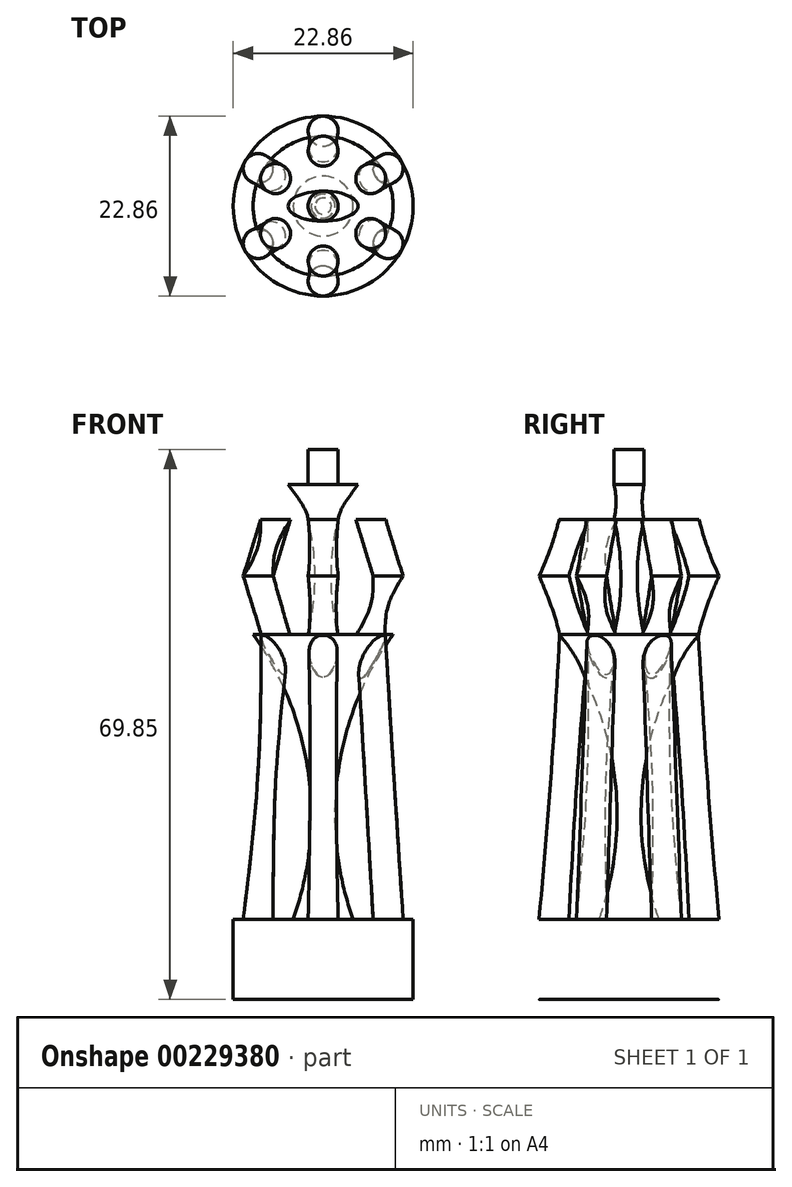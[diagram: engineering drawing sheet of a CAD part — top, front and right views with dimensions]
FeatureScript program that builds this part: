
annotation { "Feature Type Name" : "Feature", "Feature Type Description" : "" }
export const myFeature = defineFeature(function(context is Context, id is Id, definition is map)
    precondition{}
    {
        {
            var Q0;
            Q0=qCreatedBy(makeId("Top.planeOp"),FACE);
            var sketch = newSketch(context, id + "F0", { "sketchPlane" : qUnion([Q0])});
            skCircle(sketch, "E0", {"center": v(0, 0) * mm, "radius": 11.43 * mm});
            skSolve(sketch);
        }
        {
            var Q0;
            Q0=qSketchRegion(id+"F0",true);
            extrude(context, id + "F1", {"entities" : qUnion([Q0]), "depth" : 10.16 * mm});
        }
        {
            var Q0;
            Q0=makeQuery(id+"F1.opExtrude","CAP_FACE",FACE,{"disambiguationData":[OSD([sQuery(id+"F0.wireOp",EDGE,"E0")])],"isStart":false});
            var sketch = newSketch(context, id + "F2", { "sketchPlane" : qUnion([Q0])});
            skCircle(sketch, "E1", {"center": v(0, -9.53) * mm, "radius": 1.9 * mm});
            skCircle(sketch, "E2.1.0", {"center": v(8.25, -4.76) * mm, "radius": 1.9 * mm});
            skCircle(sketch, "E2.2.0", {"center": v(8.25, 4.76) * mm, "radius": 1.9 * mm});
            skCircle(sketch, "E2.3.0", {"center": v(0, 9.53) * mm, "radius": 1.9 * mm});
            skCircle(sketch, "E2.4.0", {"center": v(-8.25, 4.76) * mm, "radius": 1.9 * mm});
            skCircle(sketch, "E2.5.0", {"center": v(-8.25, -4.76) * mm, "radius": 1.9 * mm});
            skPoint(sketch, "E2.center", {"position": v(0, 0) * mm});
            skSolve(sketch);
        }
        {
            var Q0;
            Q0=qCreatedBy(makeId("Top.planeOp"),FACE);
            cPlane(context, id + "F3", {"entities" : qUnion([Q0]), "cplaneType" : CPlaneType.OFFSET, "offset" : 60.96 * mm, "width" : 152.4 * mm, "height" : 152.4 * mm});
        }
        {
            var Q0;
            Q0=qCreatedBy(makeId("Right.planeOp"),FACE);
            var sketch = newSketch(context, id + "F4", { "sketchPlane" : qUnion([Q0])});
            skLineSegment(sketch, "E3", {"start": v(0, 0) * mm, "end": v(0, 10.16) * mm});
            skLineSegment(sketch, "E4", {"start": v(0, 10.16) * mm, "end": v(0, 46.36) * mm});
            skLineSegment(sketch, "E5", {"start": v(0, 46.36) * mm, "end": v(8.9, 46.36) * mm});
            skLineSegment(sketch, "E6", {"start": v(0, 10.16) * mm, "end": v(3.81, 10.16) * mm});
            skArc(sketch, "E7", {"start": v(8.89, 46.36) * mm, "mid": v(1.9, 28.88) * mm, "end": v(3.81, 10.16) * mm});
            skSolve(sketch);
        }
        {
            var Q0;
            Q0=makeQuery(id+"F4.imprint","IMPRINT",FACE,{"disambiguationData":[TD([[makeQuery(id+"F4.imprint","IMPRINT",EDGE,{"derivedFrom":sQuery(id+"F4.wireOp",EDGE,"E4")}),-1.0]])]});
            var Q1;
            Q1=sQuery(id+"F4.wireOp",EDGE,"E4");
            revolve(context, id + "F5", {"operationType" : NewBodyOperationType.ADD, "entities" : qUnion([Q0]), "axis" : qUnion([Q1]), "revolveType" : RevolveType.FULL});
        }
        {
            var Q0;
            Q0=makeQuery(id+"F5.opRevolve","SWEPT_FACE",FACE,{"disambiguationData":[OSD([sQuery(id+"F4.wireOp",EDGE,"E5")])]});
            var sketch = newSketch(context, id + "F6", { "sketchPlane" : qUnion([Q0])});
            skCircle(sketch, "E8", {"center": v(0, -6.99) * mm, "radius": 1.83 * mm});
            skCircle(sketch, "E9.1.0", {"center": v(6.05, -3.5) * mm, "radius": 1.83 * mm});
            skCircle(sketch, "E9.2.0", {"center": v(6.05, 3.5) * mm, "radius": 1.83 * mm});
            skCircle(sketch, "E9.3.0", {"center": v(0, 6.99) * mm, "radius": 1.83 * mm});
            skCircle(sketch, "E9.4.0", {"center": v(-6.05, 3.5) * mm, "radius": 1.83 * mm});
            skCircle(sketch, "E9.5.0", {"center": v(-6.05, -3.5) * mm, "radius": 1.83 * mm});
            skPoint(sketch, "E9.center", {"position": v(0, 0) * mm});
            skSolve(sketch);
        }
        {
            var Q1;
            Q1=makeQuery(id+"F2.imprint","IMPRINT",FACE,{"disambiguationData":[TD([[makeQuery(id+"F2.imprint","IMPRINT",EDGE,{"derivedFrom":sQuery(id+"F2.wireOp",EDGE,"E2.1.0")}),1.0]])]});
            var Q2;
            Q2=makeQuery(id+"F6.imprint","IMPRINT",FACE,{"disambiguationData":[TD([[makeQuery(id+"F6.imprint","IMPRINT",EDGE,{"derivedFrom":sQuery(id+"F6.wireOp",EDGE,"E9.1.0")}),1.0]])]});
            loft(context, id + "F7", {"operationType" : NewBodyOperationType.ADD, "sheetProfilesArray" : [{ "sheetProfileEntities" : qUnion([Q1]) }, { "sheetProfileEntities" : qUnion([Q2]) }]});
        }
        {
            var Q1;
            Q1=makeQuery(id+"F2.imprint","IMPRINT",FACE,{"disambiguationData":[TD([[makeQuery(id+"F2.imprint","IMPRINT",EDGE,{"derivedFrom":sQuery(id+"F2.wireOp",EDGE,"E2.2.0")}),1.0]])]});
            var Q2;
            Q2=makeQuery(id+"F6.imprint","IMPRINT",FACE,{"disambiguationData":[TD([[makeQuery(id+"F6.imprint","IMPRINT",EDGE,{"derivedFrom":sQuery(id+"F6.wireOp",EDGE,"E9.2.0")}),1.0]])]});
            loft(context, id + "F8", {"operationType" : NewBodyOperationType.ADD, "sheetProfilesArray" : [{ "sheetProfileEntities" : qUnion([Q1]) }, { "sheetProfileEntities" : qUnion([Q2]) }]});
        }
        {
            var Q1;
            Q1=makeQuery(id+"F2.imprint","IMPRINT",FACE,{"disambiguationData":[TD([[makeQuery(id+"F2.imprint","IMPRINT",EDGE,{"derivedFrom":sQuery(id+"F2.wireOp",EDGE,"E2.5.0")}),1.0]])]});
            var Q2;
            Q2=makeQuery(id+"F6.imprint","IMPRINT",FACE,{"disambiguationData":[TD([[makeQuery(id+"F6.imprint","IMPRINT",EDGE,{"derivedFrom":sQuery(id+"F6.wireOp",EDGE,"E9.5.0")}),1.0]])]});
            loft(context, id + "F9", {"operationType" : NewBodyOperationType.ADD, "sheetProfilesArray" : [{ "sheetProfileEntities" : qUnion([Q1]) }, { "sheetProfileEntities" : qUnion([Q2]) }]});
        }
        {
            var Q1;
            Q1=makeQuery(id+"F2.imprint","IMPRINT",FACE,{"disambiguationData":[TD([[makeQuery(id+"F2.imprint","IMPRINT",EDGE,{"derivedFrom":sQuery(id+"F2.wireOp",EDGE,"E2.4.0")}),1.0]])]});
            var Q2;
            Q2=makeQuery(id+"F6.imprint","IMPRINT",FACE,{"disambiguationData":[TD([[makeQuery(id+"F6.imprint","IMPRINT",EDGE,{"derivedFrom":sQuery(id+"F6.wireOp",EDGE,"E9.4.0")}),1.0]])]});
            loft(context, id + "F10", {"operationType" : NewBodyOperationType.ADD, "sheetProfilesArray" : [{ "sheetProfileEntities" : qUnion([Q1]) }, { "sheetProfileEntities" : qUnion([Q2]) }]});
        }
        {
            var Q1;
            Q1=makeQuery(id+"F2.imprint","IMPRINT",FACE,{"disambiguationData":[TD([[makeQuery(id+"F2.imprint","IMPRINT",EDGE,{"derivedFrom":sQuery(id+"F2.wireOp",EDGE,"E2.3.0")}),1.0]])]});
            var Q2;
            Q2=makeQuery(id+"F6.imprint","IMPRINT",FACE,{"disambiguationData":[TD([[makeQuery(id+"F6.imprint","IMPRINT",EDGE,{"derivedFrom":sQuery(id+"F6.wireOp",EDGE,"E9.3.0")}),1.0]])]});
            loft(context, id + "F11", {"operationType" : NewBodyOperationType.ADD, "sheetProfilesArray" : [{ "sheetProfileEntities" : qUnion([Q1]) }, { "sheetProfileEntities" : qUnion([Q2]) }]});
        }
        {
            var Q0;
            Q0=qCreatedBy(id+"F3.planeOp",FACE);
            cPlane(context, id + "F12", {"entities" : qUnion([Q0]), "cplaneType" : CPlaneType.OFFSET, "offset" : 7.18 * mm, "oppositeDirection" : true, "width" : 152.4 * mm, "height" : 152.4 * mm});
        }
        {
            var Q0;
            Q0=qCreatedBy(id+"F12.planeOp",FACE);
            var sketch = newSketch(context, id + "F13", { "sketchPlane" : qUnion([Q0])});
            skCircle(sketch, "E10", {"center": v(0, 0) * mm, "radius": 11.43 * mm});
            skCircle(sketch, "E11", {"center": v(0, -9.53) * mm, "radius": 1.9 * mm});
            skCircle(sketch, "E12.1.0", {"center": v(8.25, -4.76) * mm, "radius": 1.9 * mm});
            skCircle(sketch, "E12.2.0", {"center": v(8.25, 4.76) * mm, "radius": 1.9 * mm});
            skCircle(sketch, "E12.3.0", {"center": v(0, 9.53) * mm, "radius": 1.9 * mm});
            skCircle(sketch, "E12.4.0", {"center": v(-8.25, 4.76) * mm, "radius": 1.9 * mm});
            skCircle(sketch, "E12.5.0", {"center": v(-8.25, -4.76) * mm, "radius": 1.9 * mm});
            skSolve(sketch);
        }
        {
            var Q1;
            Q1=makeQuery(id+"F6.imprint","IMPRINT",FACE,{"disambiguationData":[TD([[makeQuery(id+"F6.imprint","IMPRINT",EDGE,{"derivedFrom":sQuery(id+"F6.wireOp",EDGE,"E9.1.0")}),1.0]])]});
            var Q2;
            Q2=makeQuery(id+"F13.imprint","IMPRINT",FACE,{"disambiguationData":[TD([[makeQuery(id+"F13.imprint","IMPRINT",EDGE,{"derivedFrom":sQuery(id+"F13.wireOp",EDGE,"E12.1.0")}),1.0]])]});
            loft(context, id + "F14", {"operationType" : NewBodyOperationType.ADD, "sheetProfilesArray" : [{ "sheetProfileEntities" : qUnion([Q1]) }, { "sheetProfileEntities" : qUnion([Q2]) }]});
        }
        {
            var Q1;
            Q1=makeQuery(id+"F6.imprint","IMPRINT",FACE,{"disambiguationData":[TD([[makeQuery(id+"F6.imprint","IMPRINT",EDGE,{"derivedFrom":sQuery(id+"F6.wireOp",EDGE,"E9.2.0")}),1.0]])]});
            var Q2;
            Q2=makeQuery(id+"F13.imprint","IMPRINT",FACE,{"disambiguationData":[TD([[makeQuery(id+"F13.imprint","IMPRINT",EDGE,{"derivedFrom":sQuery(id+"F13.wireOp",EDGE,"E12.2.0")}),1.0]])]});
            loft(context, id + "F15", {"operationType" : NewBodyOperationType.ADD, "sheetProfilesArray" : [{ "sheetProfileEntities" : qUnion([Q1]) }, { "sheetProfileEntities" : qUnion([Q2]) }]});
        }
        {
            var Q1;
            Q1=makeQuery(id+"F6.imprint","IMPRINT",FACE,{"disambiguationData":[TD([[makeQuery(id+"F6.imprint","IMPRINT",EDGE,{"derivedFrom":sQuery(id+"F6.wireOp",EDGE,"E9.5.0")}),1.0]])]});
            var Q2;
            Q2=makeQuery(id+"F13.imprint","IMPRINT",FACE,{"disambiguationData":[TD([[makeQuery(id+"F13.imprint","IMPRINT",EDGE,{"derivedFrom":sQuery(id+"F13.wireOp",EDGE,"E12.5.0")}),1.0]])]});
            loft(context, id + "F16", {"operationType" : NewBodyOperationType.ADD, "sheetProfilesArray" : [{ "sheetProfileEntities" : qUnion([Q1]) }, { "sheetProfileEntities" : qUnion([Q2]) }]});
        }
        {
            var Q1;
            Q1=makeQuery(id+"F6.imprint","IMPRINT",FACE,{"disambiguationData":[TD([[makeQuery(id+"F6.imprint","IMPRINT",EDGE,{"derivedFrom":sQuery(id+"F6.wireOp",EDGE,"E9.4.0")}),1.0]])]});
            var Q2;
            Q2=makeQuery(id+"F13.imprint","IMPRINT",FACE,{"disambiguationData":[TD([[makeQuery(id+"F13.imprint","IMPRINT",EDGE,{"derivedFrom":sQuery(id+"F13.wireOp",EDGE,"E12.4.0")}),1.0]])]});
            loft(context, id + "F17", {"operationType" : NewBodyOperationType.ADD, "sheetProfilesArray" : [{ "sheetProfileEntities" : qUnion([Q1]) }, { "sheetProfileEntities" : qUnion([Q2]) }]});
        }
        {
            var Q1;
            Q1=makeQuery(id+"F6.imprint","IMPRINT",FACE,{"disambiguationData":[TD([[makeQuery(id+"F6.imprint","IMPRINT",EDGE,{"derivedFrom":sQuery(id+"F6.wireOp",EDGE,"E9.3.0")}),1.0]])]});
            var Q2;
            Q2=makeQuery(id+"F13.imprint","IMPRINT",FACE,{"disambiguationData":[TD([[makeQuery(id+"F13.imprint","IMPRINT",EDGE,{"derivedFrom":sQuery(id+"F13.wireOp",EDGE,"E12.3.0")}),1.0]])]});
            loft(context, id + "F18", {"operationType" : NewBodyOperationType.ADD, "sheetProfilesArray" : [{ "sheetProfileEntities" : qUnion([Q1]) }, { "sheetProfileEntities" : qUnion([Q2]) }]});
        }
        {
            var Q1;
            Q1=makeQuery(id+"F2.imprint","IMPRINT",FACE,{"disambiguationData":[TD([[makeQuery(id+"F2.imprint","IMPRINT",EDGE,{"derivedFrom":sQuery(id+"F2.wireOp",EDGE,"E1")}),1.0]])]});
            var Q2;
            Q2=makeQuery(id+"F6.imprint","IMPRINT",FACE,{"disambiguationData":[TD([[makeQuery(id+"F6.imprint","IMPRINT",EDGE,{"derivedFrom":sQuery(id+"F6.wireOp",EDGE,"E8")}),1.0]])]});
            loft(context, id + "F19", {"operationType" : NewBodyOperationType.ADD, "sheetProfilesArray" : [{ "sheetProfileEntities" : qUnion([Q1]) }, { "sheetProfileEntities" : qUnion([Q2]) }]});
        }
        {
            var Q1;
            Q1=makeQuery(id+"F6.imprint","IMPRINT",FACE,{"disambiguationData":[TD([[makeQuery(id+"F6.imprint","IMPRINT",EDGE,{"derivedFrom":sQuery(id+"F6.wireOp",EDGE,"E8")}),1.0]])]});
            var Q2;
            Q2=makeQuery(id+"F13.imprint","IMPRINT",FACE,{"disambiguationData":[TD([[makeQuery(id+"F13.imprint","IMPRINT",EDGE,{"derivedFrom":sQuery(id+"F13.wireOp",EDGE,"E11")}),1.0]])]});
            loft(context, id + "F20", {"operationType" : NewBodyOperationType.ADD, "sheetProfilesArray" : [{ "sheetProfileEntities" : qUnion([Q1]) }, { "sheetProfileEntities" : qUnion([Q2]) }]});
        }
        {
            var Q0;
            Q0=qCreatedBy(id+"F3.planeOp",FACE);
            var sketch = newSketch(context, id + "F21", { "sketchPlane" : qUnion([Q0])});
            skCircle(sketch, "E13", {"center": v(0, 0) * mm, "radius": 8.9 * mm});
            skLineSegment(sketch, "E14", {"start": v(0, -8.9) * mm, "end": v(0, -6.99) * mm});
            skCircle(sketch, "E15", {"center": v(0, -6.99) * mm, "radius": 1.9 * mm});
            skCircle(sketch, "E16.1.0", {"center": v(6.05, -3.5) * mm, "radius": 1.9 * mm});
            skCircle(sketch, "E16.2.0", {"center": v(6.05, 3.5) * mm, "radius": 1.9 * mm});
            skCircle(sketch, "E16.3.0", {"center": v(0, 6.99) * mm, "radius": 1.9 * mm});
            skCircle(sketch, "E16.4.0", {"center": v(-6.05, 3.5) * mm, "radius": 1.9 * mm});
            skCircle(sketch, "E16.5.0", {"center": v(-6.05, -3.5) * mm, "radius": 1.9 * mm});
            skLineSegment(sketch, "E17", {"start": v(0, 0) * mm, "end": v(8.9, 0) * mm});
            skSolve(sketch);
        }
        {
            var Q0;
            Q0=makeQuery(id+"F13.imprint","IMPRINT",FACE,{"disambiguationData":[TD([[makeQuery(id+"F13.imprint","IMPRINT",EDGE,{"derivedFrom":sQuery(id+"F13.wireOp",EDGE,"E12.1.0")}),1.0]])]});
            var Q1;
            Q1=makeQuery(id+"F21.imprint","IMPRINT",FACE,{"disambiguationData":[TD([[makeQuery(id+"F21.imprint","IMPRINT",EDGE,{"derivedFrom":sQuery(id+"F21.wireOp",EDGE,"E16.1.0")}),1.0]])]});
            loft(context, id + "F22", {"sheetProfilesArray" : [{ "sheetProfileEntities" : qUnion([Q0]) }, { "sheetProfileEntities" : qUnion([Q1]) }]});
        }
        {
            var Q0;
            Q0=makeQuery(id+"F13.imprint","IMPRINT",FACE,{"disambiguationData":[TD([[makeQuery(id+"F13.imprint","IMPRINT",EDGE,{"derivedFrom":sQuery(id+"F13.wireOp",EDGE,"E12.2.0")}),1.0]])]});
            var Q1;
            Q1=makeQuery(id+"F21.imprint","IMPRINT",FACE,{"disambiguationData":[TD([[makeQuery(id+"F21.imprint","IMPRINT",EDGE,{"derivedFrom":sQuery(id+"F21.wireOp",EDGE,"E16.2.0")}),1.0]])]});
            loft(context, id + "F23", {"sheetProfilesArray" : [{ "sheetProfileEntities" : qUnion([Q0]) }, { "sheetProfileEntities" : qUnion([Q1]) }]});
        }
        {
            var Q0;
            Q0=makeQuery(id+"F13.imprint","IMPRINT",FACE,{"disambiguationData":[TD([[makeQuery(id+"F13.imprint","IMPRINT",EDGE,{"derivedFrom":sQuery(id+"F13.wireOp",EDGE,"E12.5.0")}),1.0]])]});
            var Q1;
            Q1=makeQuery(id+"F21.imprint","IMPRINT",FACE,{"disambiguationData":[TD([[makeQuery(id+"F21.imprint","IMPRINT",EDGE,{"derivedFrom":sQuery(id+"F21.wireOp",EDGE,"E16.5.0")}),1.0]])]});
            loft(context, id + "F24", {"sheetProfilesArray" : [{ "sheetProfileEntities" : qUnion([Q0]) }, { "sheetProfileEntities" : qUnion([Q1]) }]});
        }
        {
            var Q0;
            Q0=makeQuery(id+"F13.imprint","IMPRINT",FACE,{"disambiguationData":[TD([[makeQuery(id+"F13.imprint","IMPRINT",EDGE,{"derivedFrom":sQuery(id+"F13.wireOp",EDGE,"E11")}),1.0]])]});
            var Q1;
            Q1=makeQuery(id+"F21.imprint","IMPRINT",FACE,{"disambiguationData":[TD([[makeQuery(id+"F21.imprint","IMPRINT",EDGE,{"derivedFrom":sQuery(id+"F21.wireOp",EDGE,"E15")}),1.0]])]});
            loft(context, id + "F25", {"sheetProfilesArray" : [{ "sheetProfileEntities" : qUnion([Q0]) }, { "sheetProfileEntities" : qUnion([Q1]) }]});
        }
        {
            var Q0;
            Q0=makeQuery(id+"F21.imprint","IMPRINT",FACE,{"disambiguationData":[TD([[makeQuery(id+"F21.imprint","IMPRINT",EDGE,{"derivedFrom":sQuery(id+"F21.wireOp",EDGE,"E16.4.0")}),1.0]])]});
            var Q1;
            Q1=makeQuery(id+"F13.imprint","IMPRINT",FACE,{"disambiguationData":[TD([[makeQuery(id+"F13.imprint","IMPRINT",EDGE,{"derivedFrom":sQuery(id+"F13.wireOp",EDGE,"E12.4.0")}),1.0]])]});
            loft(context, id + "F26", {"sheetProfilesArray" : [{ "sheetProfileEntities" : qUnion([Q0]) }, { "sheetProfileEntities" : qUnion([Q1]) }]});
        }
        {
            var Q0;
            Q0=makeQuery(id+"F13.imprint","IMPRINT",FACE,{"disambiguationData":[TD([[makeQuery(id+"F13.imprint","IMPRINT",EDGE,{"derivedFrom":sQuery(id+"F13.wireOp",EDGE,"E12.3.0")}),1.0]])]});
            var Q1;
            Q1=makeQuery(id+"F21.imprint","IMPRINT",FACE,{"disambiguationData":[TD([[makeQuery(id+"F21.imprint","IMPRINT",EDGE,{"derivedFrom":sQuery(id+"F21.wireOp",EDGE,"E16.3.0")}),1.0]])]});
            loft(context, id + "F27", {"sheetProfilesArray" : [{ "sheetProfileEntities" : qUnion([Q0]) }, { "sheetProfileEntities" : qUnion([Q1]) }]});
        }
        {
            var Q0;
            Q0=qCreatedBy(makeId("Right.planeOp"),FACE);
            var sketch = newSketch(context, id + "F28", { "sketchPlane" : qUnion([Q0])});
            skLineSegment(sketch, "E18", {"start": v(0, 0) * mm, "end": v(0, 46.35) * mm});
            skLineSegment(sketch, "E19", {"start": v(0, 46.35) * mm, "end": v(0, 60.96) * mm});
            skLineSegment(sketch, "E20", {"start": v(0, 60.96) * mm, "end": v(1.9, 60.96) * mm});
            skLineSegment(sketch, "E21", {"start": v(0, 46.35) * mm, "end": v(1.9, 46.35) * mm});
            skArc(sketch, "E22", {"start": v(1.9, 60.96) * mm, "mid": v(1.04, 53.66) * mm, "end": v(1.9, 46.35) * mm});
            skSolve(sketch);
        }
        {
            var Q0;
            Q0=makeQuery(id+"F28.imprint","IMPRINT",FACE,{"disambiguationData":[TD([[makeQuery(id+"F28.imprint","IMPRINT",EDGE,{"derivedFrom":sQuery(id+"F28.wireOp",EDGE,"E19")}),-1.0]])]});
            var Q1;
            Q1=sQuery(id+"F28.wireOp",EDGE,"E19");
            revolve(context, id + "F29", {"operationType" : NewBodyOperationType.ADD, "entities" : qUnion([Q0]), "axis" : qUnion([Q1]), "revolveType" : RevolveType.FULL});
        }
        {
            var Q0;
            Q0=qCreatedBy(id+"F3.planeOp",FACE);
            cPlane(context, id + "F30", {"entities" : qUnion([Q0]), "cplaneType" : CPlaneType.OFFSET, "offset" : 8.9 * mm, "width" : 152.4 * mm, "height" : 152.4 * mm});
        }
        {
            var Q0;
            Q0=qCreatedBy(id+"F30.planeOp",FACE);
            cPlane(context, id + "F31", {"entities" : qUnion([Q0]), "cplaneType" : CPlaneType.OFFSET, "offset" : 4.44 * mm, "oppositeDirection" : true, "width" : 152.4 * mm, "height" : 152.4 * mm});
        }
        {
            var Q0;
            Q0=qCreatedBy(id+"F31.planeOp",FACE);
            var sketch = newSketch(context, id + "F32", { "sketchPlane" : qUnion([Q0])});
            skEllipse(sketch, "E23", {"center": v(0, 0) * mm, "majorRadius": 4.45 * mm, "minorRadius": 1.9 * mm, "majorAxis": v(1, 0)});
            skSolve(sketch);
        }
        {
            var Q0;
            Q0=makeQuery(id+"F29.opRevolve","SWEPT_FACE",FACE,{"disambiguationData":[OSD([sQuery(id+"F28.wireOp",EDGE,"E20")])]});
            var Q1;
            Q1=makeQuery(id+"F32.imprint","IMPRINT",FACE,{"disambiguationData":[TD([[makeQuery(id+"F32.imprint","IMPRINT",EDGE,{"derivedFrom":sQuery(id+"F32.wireOp",EDGE,"E23")}),1.0]])]});
            loft(context, id + "F33", {"sheetProfilesArray" : [{ "sheetProfileEntities" : qUnion([Q0]) }, { "sheetProfileEntities" : qUnion([Q1]) }]});
        }
        {
            var Q0;
            Q0=makeQuery(id+"F33.opLoft","CAP_FACE",FACE,{"disambiguationData":[OSD([makeQuery(id+"F32.imprint","IMPRINT",FACE,{"disambiguationData":[TD([[makeQuery(id+"F32.imprint","IMPRINT",EDGE,{"derivedFrom":sQuery(id+"F32.wireOp",EDGE,"E23")}),1.0]])]})])],"isStart":true});
            var sketch = newSketch(context, id + "F34", { "sketchPlane" : qUnion([Q0])});
            skCircle(sketch, "E24", {"center": v(0, 0) * mm, "radius": 1.9 * mm});
            skSolve(sketch);
        }
        {
            var Q0;
            Q0=qSketchRegion(id+"F34",true);
            extrude(context, id + "F35", {"entities" : qUnion([Q0]), "operationType" : NewBodyOperationType.ADD, "depth" : 4.44 * mm});
        }
    });
